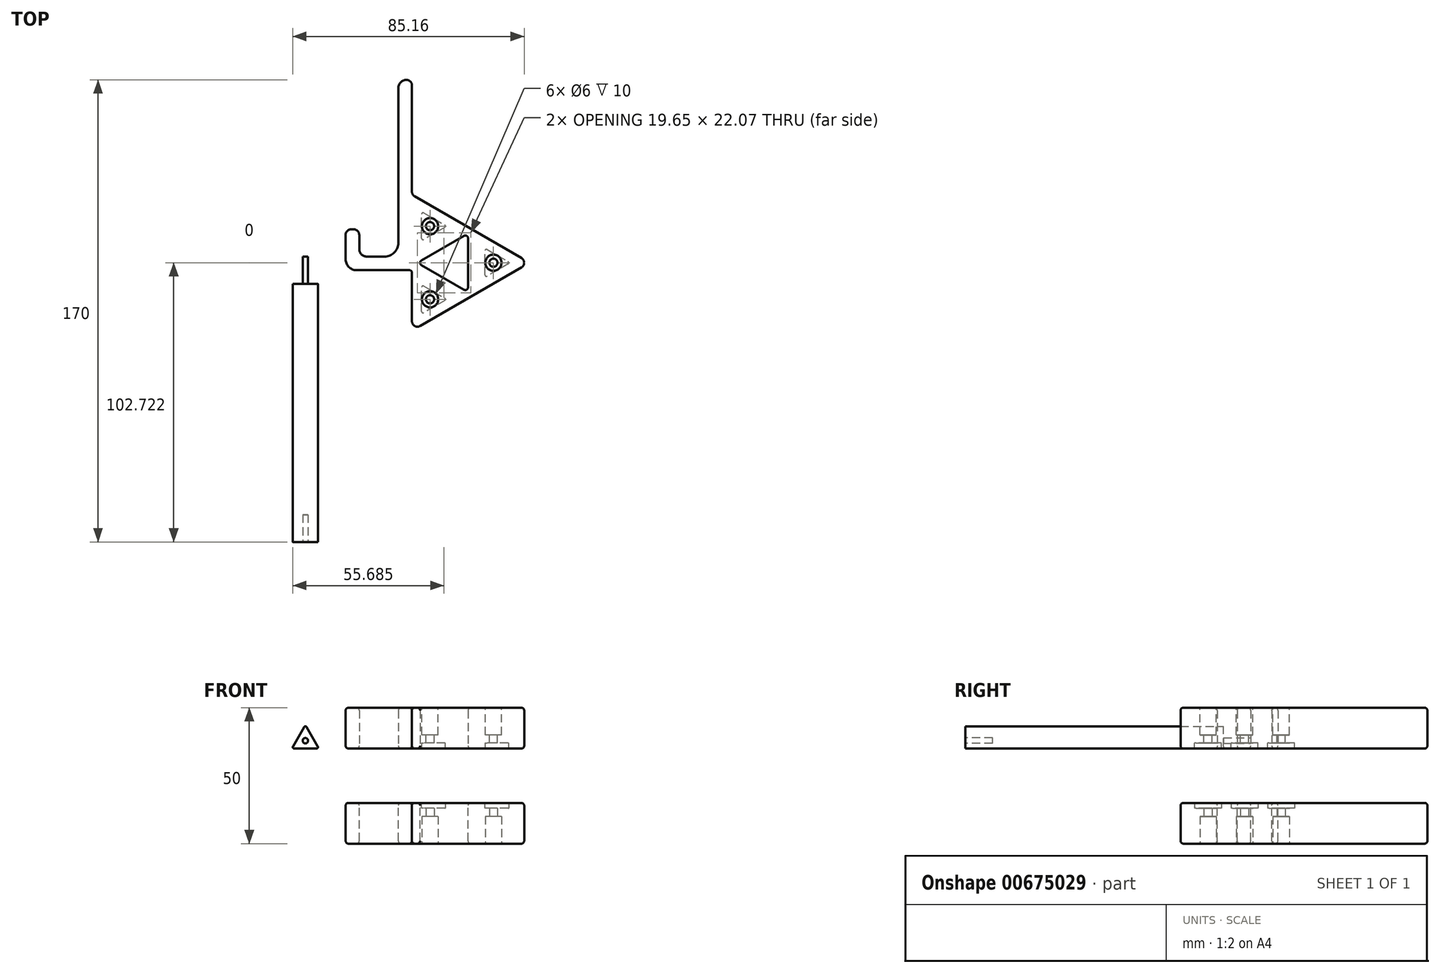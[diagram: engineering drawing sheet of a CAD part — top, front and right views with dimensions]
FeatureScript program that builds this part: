
annotation { "Feature Type Name" : "Feature", "Feature Type Description" : "" }
export const myFeature = defineFeature(function(context is Context, id is Id, definition is map)
    precondition{}
    {
        {
            var Q0;
            Q0=qCreatedBy(makeId("Top.planeOp"),FACE);
            var sketch = newSketch(context, id + "F0", { "sketchPlane" : qUnion([Q0])});
            skLineSegment(sketch, "E0", {"start": v(0, 5.1) * mm, "end": v(0, 62) * mm});
            skLineSegment(sketch, "E1", {"start": v(-5.1, 0) * mm, "end": v(-11.65, 0) * mm});
            skLineSegment(sketch, "E2", {"start": v(-14.4, 2.75) * mm, "end": v(-14.4, 8) * mm});
            skLineSegment(sketch, "E3.0", {"start": v(-19.4, -1) * mm, "end": v(-19.4, 8) * mm});
            skLineSegment(sketch, "E3.1", {"start": v(4, -5) * mm, "end": v(-15.4, -5) * mm});
            skLineSegment(sketch, "E4", {"start": v(3, 65) * mm, "end": v(3, 65) * mm});
            skLineSegment(sketch, "E5", {"start": v(-16.4, 10) * mm, "end": v(-17.4, 10) * mm});
            skPoint(sketch, "E6.visualSharp", {"position": v(0, 0) * mm});
            skArc(sketch, "E6.filletArc", {"start": v(-5.1, 0) * mm, "mid": v(-1.5, 1.5) * mm, "end": v(0, 5.1) * mm});
            skPoint(sketch, "E7.visualSharp", {"position": v(-14.4, 0) * mm});
            skArc(sketch, "E7.filletArc", {"start": v(-14.4, 2.75) * mm, "mid": v(-13.6, 0.8) * mm, "end": v(-11.65, 0) * mm});
            skPoint(sketch, "E8.visualSharp", {"position": v(-14.4, 10) * mm});
            skArc(sketch, "E8.filletArc", {"start": v(-14.4, 8) * mm, "mid": v(-14.99, 9.41) * mm, "end": v(-16.4, 10) * mm});
            skPoint(sketch, "E9.visualSharp", {"position": v(-19.4, 10) * mm});
            skArc(sketch, "E9.filletArc", {"start": v(-17.4, 10) * mm, "mid": v(-18.81, 9.41) * mm, "end": v(-19.4, 8) * mm});
            skPoint(sketch, "E10.visualSharp", {"position": v(-19.4, -5) * mm});
            skArc(sketch, "E10.filletArc", {"start": v(-19.4, -1) * mm, "mid": v(-18.23, -3.83) * mm, "end": v(-15.4, -5) * mm});
            skLineSegment(sketch, "E11", {"start": v(-8.38, 0) * mm, "end": v(-8.38, -35) * mm, "construction": true});
            skLineSegment(sketch, "E12", {"start": v(-8.38, 0) * mm, "end": v(52.25, 0) * mm, "construction": true});
            skPoint(sketch, "E13.visualSharp", {"position": v(0, 65) * mm});
            skArc(sketch, "E13.filletArc", {"start": v(3, 65) * mm, "mid": v(0.88, 64.12) * mm, "end": v(0, 62) * mm});
            skPoint(sketch, "E14.visualSharp", {"position": v(5, 65) * mm});
            skArc(sketch, "E14.filletArc", {"start": v(5, 63) * mm, "mid": v(4.41, 64.41) * mm, "end": v(3, 65) * mm});
            skLineSegment(sketch, "E15", {"start": v(8, -25.55) * mm, "end": v(45.3, -4.01) * mm});
            skLineSegment(sketch, "E16", {"start": v(45.3, -0.55) * mm, "end": v(6, 22.14) * mm});
            skLineSegment(sketch, "E17", {"start": v(26.65, 10.22) * mm, "end": v(25.65, 8.49) * mm, "construction": true});
            skLineSegment(sketch, "E18.trimOffspring", {"start": v(5, 23.88) * mm, "end": v(5, 63) * mm});
            skLineSegment(sketch, "E19", {"start": v(5, -23.81) * mm, "end": v(5, -6) * mm});
            skPoint(sketch, "E20", {"position": v(5, -2.28) * mm});
            skLineSegment(sketch, "E21", {"start": v(5, -2.28) * mm, "end": v(7, -2.28) * mm, "construction": true});
            skLineSegment(sketch, "E22", {"start": v(26.65, -14.78) * mm, "end": v(25.65, -13.05) * mm, "construction": true});
            skLineSegment(sketch, "E23", {"start": v(25.65, -11.31) * mm, "end": v(25.65, 6.76) * mm});
            skLineSegment(sketch, "E24", {"start": v(24.15, 7.62) * mm, "end": v(8.5, -1.41) * mm});
            skLineSegment(sketch, "E25", {"start": v(8.5, -3.14) * mm, "end": v(24.15, -12.18) * mm});
            skLineSegment(sketch, "E26", {"start": v(-8.38, -35) * mm, "end": v(5, -27.28) * mm, "construction": true});
            skLineSegment(sketch, "E27", {"start": v(48.3, -2.28) * mm, "end": v(52.25, 0) * mm, "construction": true});
            skLineSegment(sketch, "E28", {"start": v(5, 0) * mm, "end": v(5, -2.28) * mm, "construction": true});
            skPoint(sketch, "E29", {"position": v(5, -5) * mm});
            skPoint(sketch, "E30.visualSharp", {"position": v(48.3, -2.28) * mm});
            skArc(sketch, "E30.filletArc", {"start": v(45.3, -4.01) * mm, "mid": v(46.3, -2.28) * mm, "end": v(45.3, -0.55) * mm});
            skPoint(sketch, "E31.visualSharp", {"position": v(5, -27.28) * mm});
            skArc(sketch, "E31.filletArc", {"start": v(5, -23.81) * mm, "mid": v(6, -25.55) * mm, "end": v(8, -25.55) * mm});
            skPoint(sketch, "E32.visualSharp", {"position": v(25.65, -13.05) * mm});
            skArc(sketch, "E32.filletArc", {"start": v(24.15, -12.18) * mm, "mid": v(25.15, -12.18) * mm, "end": v(25.65, -11.31) * mm});
            skPoint(sketch, "E33.visualSharp", {"position": v(7, -2.28) * mm});
            skArc(sketch, "E33.filletArc", {"start": v(8.5, -1.41) * mm, "mid": v(8, -2.28) * mm, "end": v(8.5, -3.14) * mm});
            skPoint(sketch, "E34.visualSharp", {"position": v(25.65, 8.49) * mm});
            skArc(sketch, "E34.filletArc", {"start": v(25.65, 6.76) * mm, "mid": v(25.15, 7.62) * mm, "end": v(24.15, 7.62) * mm});
            skPoint(sketch, "E35.visualSharp", {"position": v(5, 22.72) * mm});
            skArc(sketch, "E35.filletArc", {"start": v(5, 23.88) * mm, "mid": v(5.27, 22.88) * mm, "end": v(6, 22.14) * mm});
            skArc(sketch, "E36.filletArc", {"start": v(5, -6) * mm, "mid": v(4.7, -5.3) * mm, "end": v(4, -5) * mm});
            skLineSegment(sketch, "E37", {"start": v(7, -2.28) * mm, "end": v(25.65, 8.49) * mm, "construction": true});
            skLineSegment(sketch, "E38", {"start": v(25.65, 8.49) * mm, "end": v(25.65, -13.05) * mm, "construction": true});
            skLineSegment(sketch, "E39", {"start": v(25.65, -13.05) * mm, "end": v(7, -2.28) * mm, "construction": true});
            skLineSegment(sketch, "E40", {"start": v(5, 22.72) * mm, "end": v(16.33, 3.1) * mm, "construction": true});
            skLineSegment(sketch, "E41", {"start": v(5, -27.28) * mm, "end": v(16.33, -7.66) * mm, "construction": true});
            skLineSegment(sketch, "E42", {"start": v(48.3, -2.28) * mm, "end": v(25.65, -2.28) * mm, "construction": true});
            skPoint(sketch, "E43", {"position": v(10.66, 12.91) * mm});
            skPoint(sketch, "E44", {"position": v(10.66, -17.47) * mm});
            skPoint(sketch, "E45", {"position": v(36.98, -2.28) * mm});
            skPoint(sketch, "E46", {"position": v(11.66, -15.74) * mm});
            skPoint(sketch, "E47", {"position": v(11.66, 11.18) * mm});
            skPoint(sketch, "E48", {"position": v(34.98, -2.28) * mm});
            skSolve(sketch);
        }
        {
            var Q0;
            Q0=makeQuery(id+"F0.imprint","IMPRINT",FACE,{"disambiguationData":[TD([[makeQuery(id+"F0.imprint","IMPRINT",EDGE,{"derivedFrom":sQuery(id+"F0.wireOp",EDGE,"E0")}),-1.0]])]});
            extrude(context, id + "F1", {"entities" : qUnion([Q0]), "depth" : 15 * mm, "offsetDistance" : 25 * mm});
        }
        {
            var Q0;
            Q0=makeQuery(id+"F1.opExtrude","CAP_EDGE",EDGE,{"disambiguationData":[OSD([sQuery(id+"F0.wireOp",EDGE,"E0")])],"isStart":true});
            var Q1;
            Q1=makeQuery(id+"F1.opExtrude","CAP_EDGE",EDGE,{"disambiguationData":[OSD([sQuery(id+"F0.wireOp",EDGE,"E13.filletArc")])],"isStart":true});
            var Q2;
            Q2=makeQuery(id+"F1.opExtrude","CAP_EDGE",EDGE,{"disambiguationData":[OSD([sQuery(id+"F0.wireOp",EDGE,"E1")])],"isStart":false});
            var Q3;
            Q3=makeQuery(id+"F1.opExtrude","CAP_EDGE",EDGE,{"disambiguationData":[OSD([sQuery(id+"F0.wireOp",EDGE,"E23")])],"isStart":true});
            var Q4;
            Q4=makeQuery(id+"F1.opExtrude","CAP_EDGE",EDGE,{"disambiguationData":[OSD([sQuery(id+"F0.wireOp",EDGE,"E25")])],"isStart":false});
            fillet(context, id + "F2", {"entities" : qUnion([Q0, Q1, Q2, Q3, Q4]), "radius" : 1 * mm, "tangentPropagation" : true, "allowEdgeOverflow" : false});
        }
        {
            var Q0;
            Q0=makeQuery(id+"F1.opExtrude","CAP_FACE",FACE,{"disambiguationData":[OSD([sQuery(id+"F0.wireOp",EDGE,"E0"),sQuery(id+"F0.wireOp",EDGE,"E1"),sQuery(id+"F0.wireOp",EDGE,"E2"),sQuery(id+"F0.wireOp",EDGE,"E3.0"),sQuery(id+"F0.wireOp",EDGE,"E3.1"),sQuery(id+"F0.wireOp",EDGE,"E5"),sQuery(id+"F0.wireOp",EDGE,"E6.filletArc"),sQuery(id+"F0.wireOp",EDGE,"E7.filletArc"),sQuery(id+"F0.wireOp",EDGE,"E8.filletArc"),sQuery(id+"F0.wireOp",EDGE,"E9.filletArc"),sQuery(id+"F0.wireOp",EDGE,"E10.filletArc"),sQuery(id+"F0.wireOp",EDGE,"E13.filletArc"),sQuery(id+"F0.wireOp",EDGE,"E14.filletArc"),sQuery(id+"F0.wireOp",EDGE,"E15"),sQuery(id+"F0.wireOp",EDGE,"E16"),sQuery(id+"F0.wireOp",EDGE,"E18.trimOffspring"),sQuery(id+"F0.wireOp",EDGE,"E19"),sQuery(id+"F0.wireOp",EDGE,"E23"),sQuery(id+"F0.wireOp",EDGE,"E24"),sQuery(id+"F0.wireOp",EDGE,"E25"),sQuery(id+"F0.wireOp",EDGE,"E30.filletArc"),sQuery(id+"F0.wireOp",EDGE,"E31.filletArc"),sQuery(id+"F0.wireOp",EDGE,"E32.filletArc"),sQuery(id+"F0.wireOp",EDGE,"E33.filletArc"),sQuery(id+"F0.wireOp",EDGE,"E34.filletArc"),sQuery(id+"F0.wireOp",EDGE,"E35.filletArc"),sQuery(id+"F0.wireOp",EDGE,"E36.filletArc")])],"isStart":false});
            var sketch = newSketch(context, id + "F3", { "sketchPlane" : qUnion([Q0])});
            skPoint(sketch, "E49.0", {"position": v(11.66, 11.18) * mm});
            skPoint(sketch, "E49.1", {"position": v(11.66, -15.74) * mm});
            skPoint(sketch, "E49.2", {"position": v(34.98, -2.28) * mm});
            skSolve(sketch);
        }
        {
            var Q0;
            Q0=sQuery(id+"F3.wireOp",VERTEX,"E49.0");
            var Q1;
            Q1=sQuery(id+"F3.wireOp",VERTEX,"E49.1");
            var Q2;
            Q2=sQuery(id+"F3.wireOp",VERTEX,"E49.2");
            var Q3;
            Q3=makeQuery(id+"F1.opExtrude","SWEPT_BODY",BODY,{"disambiguationData":[OSD([sQuery(id+"F0.wireOp",EDGE,"E0"),sQuery(id+"F0.wireOp",EDGE,"E1"),sQuery(id+"F0.wireOp",EDGE,"E2"),sQuery(id+"F0.wireOp",EDGE,"E3.0"),sQuery(id+"F0.wireOp",EDGE,"E3.1"),sQuery(id+"F0.wireOp",EDGE,"E5"),sQuery(id+"F0.wireOp",EDGE,"E6.filletArc"),sQuery(id+"F0.wireOp",EDGE,"E7.filletArc"),sQuery(id+"F0.wireOp",EDGE,"E8.filletArc"),sQuery(id+"F0.wireOp",EDGE,"E9.filletArc"),sQuery(id+"F0.wireOp",EDGE,"E10.filletArc"),sQuery(id+"F0.wireOp",EDGE,"E13.filletArc"),sQuery(id+"F0.wireOp",EDGE,"E14.filletArc"),sQuery(id+"F0.wireOp",EDGE,"E15"),sQuery(id+"F0.wireOp",EDGE,"E16"),sQuery(id+"F0.wireOp",EDGE,"E18.trimOffspring"),sQuery(id+"F0.wireOp",EDGE,"E19"),sQuery(id+"F0.wireOp",EDGE,"E23"),sQuery(id+"F0.wireOp",EDGE,"E24"),sQuery(id+"F0.wireOp",EDGE,"E25"),sQuery(id+"F0.wireOp",EDGE,"E30.filletArc"),sQuery(id+"F0.wireOp",EDGE,"E31.filletArc"),sQuery(id+"F0.wireOp",EDGE,"E32.filletArc"),sQuery(id+"F0.wireOp",EDGE,"E33.filletArc"),sQuery(id+"F0.wireOp",EDGE,"E34.filletArc"),sQuery(id+"F0.wireOp",EDGE,"E35.filletArc"),sQuery(id+"F0.wireOp",EDGE,"E36.filletArc")])]});
            hole(context, id + "F4", {"style" : HoleStyle.C_BORE, "endStyle" : HoleEndStyle.THROUGH, "holeDiameter" : 3 * mm, "cBoreDiameter" : 6 * mm, "cBoreDepth" : 10 * mm, "majorDiameter" : 5 * mm, "isTappedThrough" : true, "tappedDepth" : 12 * mm, "tapClearance" : 3, "locations" : qUnion([Q0, Q1, Q2]), "scope" : qUnion([Q3])});
        }
        {
            var Q0;
            Q0=qCreatedBy(makeId("Front.planeOp"),FACE);
            var sketch = newSketch(context, id + "F5", { "sketchPlane" : qUnion([Q0])});
            skLineSegment(sketch, "E50", {"start": v(-39.23, 0) * mm, "end": v(-34.23, 8.66) * mm});
            skLineSegment(sketch, "E51", {"start": v(-34.23, 8.66) * mm, "end": v(-29.23, 0) * mm});
            skLineSegment(sketch, "E52", {"start": v(-29.23, 0) * mm, "end": v(-39.23, 0) * mm});
            skSolve(sketch);
        }
        {
            var Q0;
            Q0=makeQuery(id+"F5.imprint","IMPRINT",FACE,{"disambiguationData":[TD([[makeQuery(id+"F5.imprint","IMPRINT",EDGE,{"derivedFrom":sQuery(id+"F5.wireOp",EDGE,"E50")}),-1.0]])]});
            extrude(context, id + "F6", {"entities" : qUnion([Q0]), "depth" : 105 * mm, "offsetDistance" : 25 * mm});
        }
        {
            var Q0;
            Q0=makeQuery(id+"F6.opExtrude","SWEPT_EDGE",EDGE,{"disambiguationData":[OSD([sQuery(id+"F5.wireOp",EDGE,"E50"),sQuery(id+"F5.wireOp",EDGE,"E51")])]});
            var Q1;
            Q1=makeQuery(id+"F6.opExtrude","SWEPT_EDGE",EDGE,{"disambiguationData":[OSD([sQuery(id+"F5.wireOp",EDGE,"E51"),sQuery(id+"F5.wireOp",EDGE,"E52")])]});
            var Q2;
            Q2=makeQuery(id+"F6.opExtrude","SWEPT_EDGE",EDGE,{"disambiguationData":[OSD([sQuery(id+"F5.wireOp",EDGE,"E50"),sQuery(id+"F5.wireOp",EDGE,"E52")])]});
            fillet(context, id + "F7", {"entities" : qUnion([Q0, Q1, Q2]), "radius" : 0.5 * mm, "tangentPropagation" : true, "allowEdgeOverflow" : false});
        }
        {
            var Q0;
            Q0=makeQuery(id+"F6.opExtrude","CAP_FACE",FACE,{"disambiguationData":[OSD([sQuery(id+"F5.wireOp",EDGE,"E50"),sQuery(id+"F5.wireOp",EDGE,"E51"),sQuery(id+"F5.wireOp",EDGE,"E52")])],"isStart":false});
            var sketch = newSketch(context, id + "F8", { "sketchPlane" : qUnion([Q0])});
            skPoint(sketch, "E53.0", {"position": v(-31.73, 4.33) * mm});
            skPoint(sketch, "E53.1", {"position": v(-36.73, 4.33) * mm});
            skPoint(sketch, "E53.2", {"position": v(-34.23, 0) * mm});
            skLineSegment(sketch, "E54.0", {"start": v(-30.1, 0) * mm, "end": v(-38.36, 0) * mm, "construction": true});
            skLineSegment(sketch, "E54.1", {"start": v(-33.8, 7.91) * mm, "end": v(-29.66, 0.75) * mm, "construction": true});
            skLineSegment(sketch, "E54.2", {"start": v(-38.8, 0.75) * mm, "end": v(-34.66, 7.91) * mm, "construction": true});
            skLineSegment(sketch, "E55", {"start": v(-31.73, 4.33) * mm, "end": v(-34.23, 2.89) * mm, "construction": true});
            skLineSegment(sketch, "E56", {"start": v(-36.73, 4.33) * mm, "end": v(-34.23, 2.89) * mm, "construction": true});
            skLineSegment(sketch, "E57", {"start": v(-34.23, 0) * mm, "end": v(-34.23, 2.89) * mm, "construction": true});
            skPoint(sketch, "E58", {"position": v(-34.23, 2.89) * mm});
            skCircle(sketch, "E59", {"center": v(-34.23, 2.89) * mm, "radius": 1 * mm});
            skSolve(sketch);
        }
        {
            var Q0;
            Q0=makeQuery(id+"F6.opExtrude","CAP_FACE",FACE,{"disambiguationData":[OSD([sQuery(id+"F5.wireOp",EDGE,"E50"),sQuery(id+"F5.wireOp",EDGE,"E51"),sQuery(id+"F5.wireOp",EDGE,"E52")])],"isStart":true});
            var sketch = newSketch(context, id + "F9", { "sketchPlane" : qUnion([Q0])});
            skLineSegment(sketch, "E60.0", {"start": v(30.1, 0) * mm, "end": v(38.36, 0) * mm, "construction": true});
            skPoint(sketch, "E60.1", {"position": v(34.23, 0) * mm});
            skLineSegment(sketch, "E60.2", {"start": v(34.23, 0) * mm, "end": v(34.23, 2.89) * mm, "construction": true});
            skCircle(sketch, "E60.3", {"center": v(34.23, 2.89) * mm, "radius": 1 * mm});
            skLineSegment(sketch, "E60.4", {"start": v(36.73, 4.33) * mm, "end": v(34.23, 2.89) * mm, "construction": true});
            skLineSegment(sketch, "E60.5", {"start": v(31.73, 4.33) * mm, "end": v(34.23, 2.89) * mm, "construction": true});
            skLineSegment(sketch, "E60.6", {"start": v(33.8, 7.91) * mm, "end": v(29.66, 0.75) * mm, "construction": true});
            skLineSegment(sketch, "E60.7", {"start": v(38.8, 0.75) * mm, "end": v(34.66, 7.91) * mm, "construction": true});
            skPoint(sketch, "E60.8", {"position": v(34.23, 2.89) * mm});
            skSolve(sketch);
        }
        {
            var Q0;
            Q0=makeQuery(id+"F9.imprint","IMPRINT",FACE,{"disambiguationData":[TD([[makeQuery(id+"F9.imprint","IMPRINT",EDGE,{"derivedFrom":sQuery(id+"F9.wireOp",EDGE,"E60.3")}),-1.0]])]});
            extrude(context, id + "F10", {"entities" : qUnion([Q0]), "operationType" : NewBodyOperationType.REMOVE, "oppositeDirection" : true, "depth" : 10 * mm, "offsetDistance" : 25 * mm});
        }
        {
            var Q0;
            Q0=makeQuery(id+"F8.imprint","IMPRINT",FACE,{"disambiguationData":[TD([[makeQuery(id+"F8.imprint","IMPRINT",EDGE,{"derivedFrom":sQuery(id+"F8.wireOp",EDGE,"E59")}),1.0]])]});
            extrude(context, id + "F11", {"entities" : qUnion([Q0]), "operationType" : NewBodyOperationType.REMOVE, "oppositeDirection" : true, "depth" : 10 * mm, "offsetDistance" : 25 * mm});
        }
        {
            var Q0;
            Q0=makeQuery(id+"F0.imprint","IMPRINT",FACE,{"disambiguationData":[TD([[makeQuery(id+"F0.imprint","IMPRINT",EDGE,{"derivedFrom":sQuery(id+"F0.wireOp",EDGE,"E0")}),-1.0]])]});
            var sketch = newSketch(context, id + "F12", { "sketchPlane" : qUnion([Q0])});
            skPoint(sketch, "E61.0", {"position": v(11.66, -15.74) * mm});
            skPoint(sketch, "E61.2", {"position": v(34.98, -2.28) * mm});
            skLineSegment(sketch, "E62.0", {"start": v(17.44, -15.74) * mm, "end": v(8.78, -20.74) * mm, "construction": true});
            skLineSegment(sketch, "E62.1", {"start": v(8.78, -10.74) * mm, "end": v(17.44, -15.74) * mm, "construction": true});
            skLineSegment(sketch, "E62.2", {"start": v(8.78, -20.74) * mm, "end": v(8.78, -10.74) * mm, "construction": true});
            skLineSegment(sketch, "E63", {"start": v(13.1, -13.24) * mm, "end": v(11.66, -15.74) * mm, "construction": true});
            skLineSegment(sketch, "E64", {"start": v(8.78, -15.74) * mm, "end": v(11.66, -15.74) * mm, "construction": true});
            skLineSegment(sketch, "E65", {"start": v(13.1, -18.24) * mm, "end": v(11.66, -15.74) * mm, "construction": true});
            skLineSegment(sketch, "E66.0", {"start": v(17.84, -15.74) * mm, "end": v(8.58, -21.08) * mm});
            skLineSegment(sketch, "E66.1", {"start": v(8.58, -10.4) * mm, "end": v(17.84, -15.74) * mm});
            skLineSegment(sketch, "E66.2", {"start": v(8.58, -21.08) * mm, "end": v(8.58, -10.4) * mm});
            skPoint(sketch, "E67.0", {"position": v(11.66, 11.18) * mm});
            skLineSegment(sketch, "E68.0", {"start": v(40.75, -2.28) * mm, "end": v(32.09, -7.28) * mm, "construction": true});
            skLineSegment(sketch, "E68.1", {"start": v(32.09, 2.72) * mm, "end": v(40.75, -2.28) * mm, "construction": true});
            skLineSegment(sketch, "E68.2", {"start": v(32.09, -7.28) * mm, "end": v(32.09, 2.72) * mm, "construction": true});
            skLineSegment(sketch, "E69", {"start": v(36.42, 0.22) * mm, "end": v(34.98, -2.28) * mm, "construction": true});
            skLineSegment(sketch, "E70", {"start": v(32.09, -2.28) * mm, "end": v(34.98, -2.28) * mm, "construction": true});
            skLineSegment(sketch, "E71", {"start": v(36.42, -4.78) * mm, "end": v(34.98, -2.28) * mm, "construction": true});
            skLineSegment(sketch, "E72.0", {"start": v(41.15, -2.28) * mm, "end": v(31.89, -7.62) * mm});
            skLineSegment(sketch, "E72.1", {"start": v(31.89, 3.07) * mm, "end": v(41.15, -2.28) * mm});
            skLineSegment(sketch, "E72.2", {"start": v(31.89, -7.62) * mm, "end": v(31.89, 3.07) * mm});
            skLineSegment(sketch, "E73.0", {"start": v(17.44, 11.18) * mm, "end": v(8.78, 6.18) * mm, "construction": true});
            skLineSegment(sketch, "E73.1", {"start": v(8.78, 16.18) * mm, "end": v(17.44, 11.18) * mm, "construction": true});
            skLineSegment(sketch, "E73.2", {"start": v(8.78, 6.18) * mm, "end": v(8.78, 16.18) * mm, "construction": true});
            skLineSegment(sketch, "E74", {"start": v(13.1, 13.68) * mm, "end": v(11.66, 11.18) * mm, "construction": true});
            skLineSegment(sketch, "E75", {"start": v(8.78, 11.18) * mm, "end": v(11.66, 11.18) * mm, "construction": true});
            skLineSegment(sketch, "E76", {"start": v(13.1, 8.68) * mm, "end": v(11.66, 11.18) * mm, "construction": true});
            skLineSegment(sketch, "E77.0", {"start": v(17.84, 11.18) * mm, "end": v(8.58, 5.84) * mm});
            skLineSegment(sketch, "E77.1", {"start": v(8.58, 16.53) * mm, "end": v(17.84, 11.18) * mm});
            skLineSegment(sketch, "E77.2", {"start": v(8.58, 5.84) * mm, "end": v(8.58, 16.53) * mm});
            skSolve(sketch);
        }
        {
            var Q0;
            Q0=makeQuery(id+"F12.imprint","IMPRINT",FACE,{"disambiguationData":[TD([[makeQuery(id+"F12.imprint","IMPRINT",EDGE,{"derivedFrom":sQuery(id+"F12.wireOp",EDGE,"E66.0")}),-1.0]])]});
            var Q1;
            Q1=makeQuery(id+"F12.imprint","IMPRINT",FACE,{"disambiguationData":[TD([[makeQuery(id+"F12.imprint","IMPRINT",EDGE,{"derivedFrom":sQuery(id+"F12.wireOp",EDGE,"E72.0")}),-1.0]])]});
            var Q2;
            Q2=makeQuery(id+"F12.imprint","IMPRINT",FACE,{"disambiguationData":[TD([[makeQuery(id+"F12.imprint","IMPRINT",EDGE,{"derivedFrom":sQuery(id+"F12.wireOp",EDGE,"E77.0")}),-1.0]])]});
            extrude(context, id + "F13", {"entities" : qUnion([Q0, Q1, Q2]), "operationType" : NewBodyOperationType.REMOVE, "depth" : 2 * mm, "offsetDistance" : 25 * mm});
        }
        {
            var Q0;
            Q0=makeQuery(id+"F13.boolean.opBoolean","COPY",EDGE,{"derivedFrom":makeQuery(id+"F13.opExtrude","SWEPT_EDGE",EDGE,{"disambiguationData":[OSD([sQuery(id+"F12.wireOp",EDGE,"E66.0"),sQuery(id+"F12.wireOp",EDGE,"E66.2")])]})});
            var Q1;
            Q1=makeQuery(id+"F13.boolean.opBoolean","COPY",EDGE,{"derivedFrom":makeQuery(id+"F13.opExtrude","SWEPT_EDGE",EDGE,{"disambiguationData":[OSD([sQuery(id+"F12.wireOp",EDGE,"E66.0"),sQuery(id+"F12.wireOp",EDGE,"E66.1")])]})});
            var Q2;
            Q2=makeQuery(id+"F13.boolean.opBoolean","COPY",EDGE,{"derivedFrom":makeQuery(id+"F13.opExtrude","SWEPT_EDGE",EDGE,{"disambiguationData":[OSD([sQuery(id+"F12.wireOp",EDGE,"E66.1"),sQuery(id+"F12.wireOp",EDGE,"E66.2")])]})});
            var Q3;
            Q3=makeQuery(id+"F13.boolean.opBoolean","COPY",EDGE,{"derivedFrom":makeQuery(id+"F13.opExtrude","SWEPT_EDGE",EDGE,{"disambiguationData":[OSD([sQuery(id+"F12.wireOp",EDGE,"E77.1"),sQuery(id+"F12.wireOp",EDGE,"E77.2")])]})});
            var Q4;
            Q4=makeQuery(id+"F13.boolean.opBoolean","COPY",EDGE,{"derivedFrom":makeQuery(id+"F13.opExtrude","SWEPT_EDGE",EDGE,{"disambiguationData":[OSD([sQuery(id+"F12.wireOp",EDGE,"E77.0"),sQuery(id+"F12.wireOp",EDGE,"E77.2")])]})});
            var Q5;
            Q5=makeQuery(id+"F13.boolean.opBoolean","COPY",EDGE,{"derivedFrom":makeQuery(id+"F13.opExtrude","SWEPT_EDGE",EDGE,{"disambiguationData":[OSD([sQuery(id+"F12.wireOp",EDGE,"E77.0"),sQuery(id+"F12.wireOp",EDGE,"E77.1")])]})});
            var Q6;
            Q6=makeQuery(id+"F13.boolean.opBoolean","COPY",EDGE,{"derivedFrom":makeQuery(id+"F13.opExtrude","SWEPT_EDGE",EDGE,{"disambiguationData":[OSD([sQuery(id+"F12.wireOp",EDGE,"E72.0"),sQuery(id+"F12.wireOp",EDGE,"E72.1")])]})});
            var Q7;
            Q7=makeQuery(id+"F13.boolean.opBoolean","COPY",EDGE,{"derivedFrom":makeQuery(id+"F13.opExtrude","SWEPT_EDGE",EDGE,{"disambiguationData":[OSD([sQuery(id+"F12.wireOp",EDGE,"E72.1"),sQuery(id+"F12.wireOp",EDGE,"E72.2")])]})});
            var Q8;
            Q8=makeQuery(id+"F13.boolean.opBoolean","COPY",EDGE,{"derivedFrom":makeQuery(id+"F13.opExtrude","SWEPT_EDGE",EDGE,{"disambiguationData":[OSD([sQuery(id+"F12.wireOp",EDGE,"E72.0"),sQuery(id+"F12.wireOp",EDGE,"E72.2")])]})});
            fillet(context, id + "F14", {"entities" : qUnion([Q0, Q1, Q2, Q3, Q4, Q5, Q6, Q7, Q8]), "radius" : 0.5 * mm, "tangentPropagation" : true, "allowEdgeOverflow" : false});
        }
        {
            var Q0;
            Q0=qCreatedBy(makeId("Top.planeOp"),FACE);
            cPlane(context, id + "F15", {"entities" : qUnion([Q0]), "cplaneType" : CPlaneType.OFFSET, "offset" : 10 * mm, "oppositeDirection" : true, "width" : 150 * mm, "height" : 150 * mm});
        }
        {
            var Q0;
            Q0=makeQuery(id+"F1.opExtrude","SWEPT_BODY",BODY,{"disambiguationData":[OSD([sQuery(id+"F0.wireOp",EDGE,"E0"),sQuery(id+"F0.wireOp",EDGE,"E1"),sQuery(id+"F0.wireOp",EDGE,"E2"),sQuery(id+"F0.wireOp",EDGE,"E3.0"),sQuery(id+"F0.wireOp",EDGE,"E3.1"),sQuery(id+"F0.wireOp",EDGE,"E5"),sQuery(id+"F0.wireOp",EDGE,"E6.filletArc"),sQuery(id+"F0.wireOp",EDGE,"E7.filletArc"),sQuery(id+"F0.wireOp",EDGE,"E8.filletArc"),sQuery(id+"F0.wireOp",EDGE,"E9.filletArc"),sQuery(id+"F0.wireOp",EDGE,"E10.filletArc"),sQuery(id+"F0.wireOp",EDGE,"E13.filletArc"),sQuery(id+"F0.wireOp",EDGE,"E14.filletArc"),sQuery(id+"F0.wireOp",EDGE,"E15"),sQuery(id+"F0.wireOp",EDGE,"E16"),sQuery(id+"F0.wireOp",EDGE,"E18.trimOffspring"),sQuery(id+"F0.wireOp",EDGE,"E19"),sQuery(id+"F0.wireOp",EDGE,"E23"),sQuery(id+"F0.wireOp",EDGE,"E24"),sQuery(id+"F0.wireOp",EDGE,"E25"),sQuery(id+"F0.wireOp",EDGE,"E30.filletArc"),sQuery(id+"F0.wireOp",EDGE,"E31.filletArc"),sQuery(id+"F0.wireOp",EDGE,"E32.filletArc"),sQuery(id+"F0.wireOp",EDGE,"E33.filletArc"),sQuery(id+"F0.wireOp",EDGE,"E34.filletArc"),sQuery(id+"F0.wireOp",EDGE,"E35.filletArc"),sQuery(id+"F0.wireOp",EDGE,"E36.filletArc")])]});
            var Q1;
            Q1=qCreatedBy(id+"F15.planeOp",FACE);
            mirror(context, id + "F16", {"entities" : qUnion([Q0]), "mirrorPlane" : qUnion([Q1])});
        }
    });
